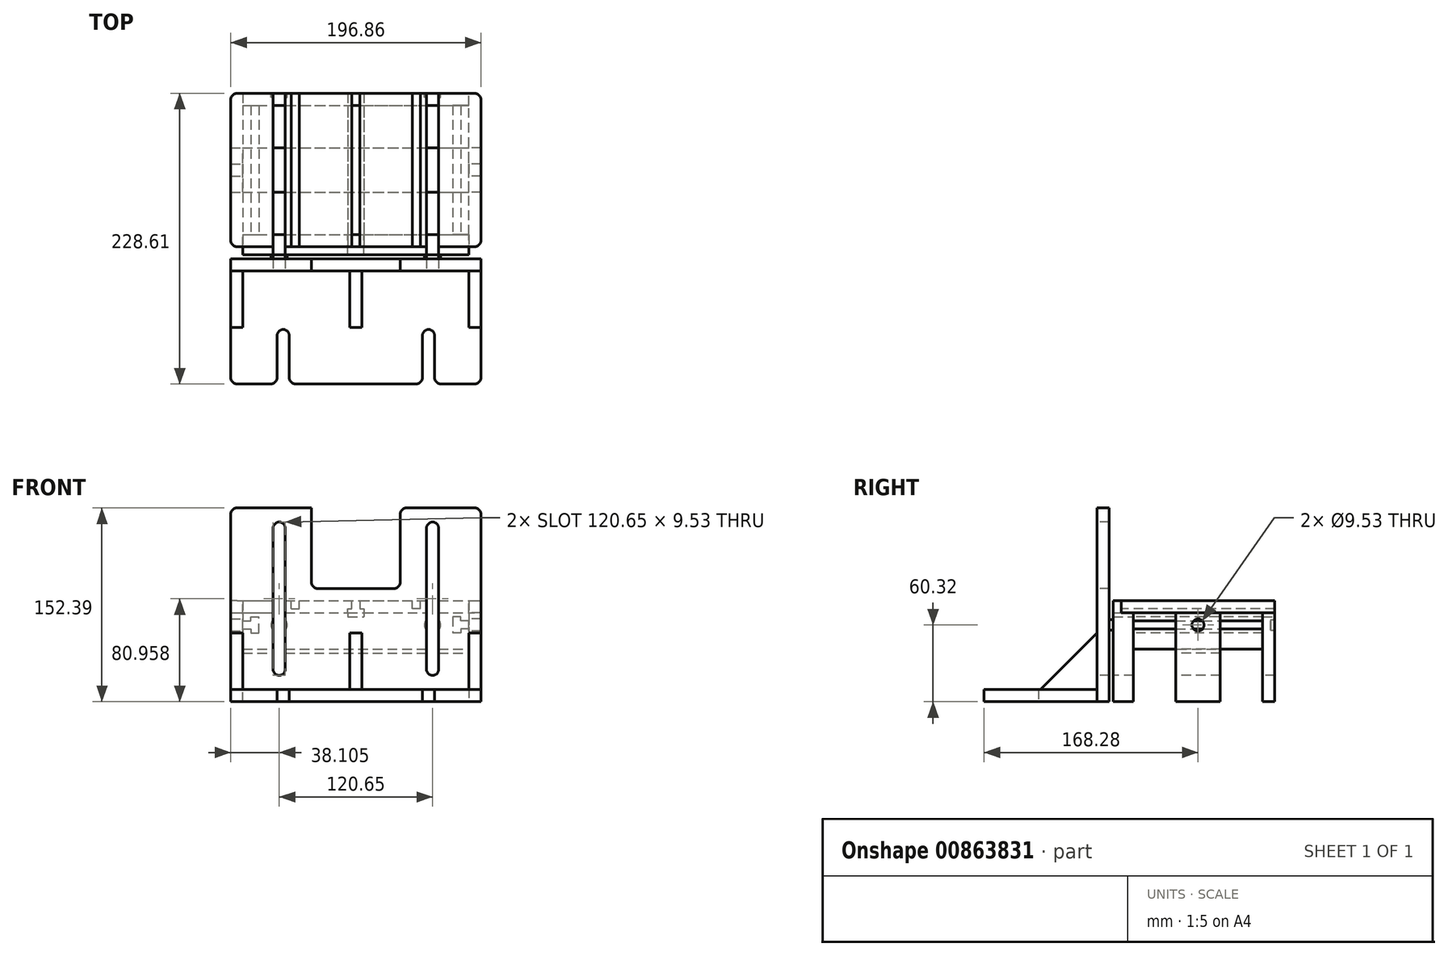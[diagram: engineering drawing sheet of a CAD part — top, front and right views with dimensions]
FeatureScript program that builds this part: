
annotation { "Feature Type Name" : "Feature", "Feature Type Description" : "" }
export const myFeature = defineFeature(function(context is Context, id is Id, definition is map)
    precondition{}
    {
        {
            var Q0;
            Q0=qCreatedBy(makeId("Top.planeOp"),FACE);
            var sketch = newSketch(context, id + "F0", { "sketchPlane" : qUnion([Q0])});
            skLineSegment(sketch, "E0.bottom", {"start": v(-98.42, 60.33) * mm, "end": v(98.43, 60.33) * mm});
            skLineSegment(sketch, "E0.top", {"start": v(-98.43, -60.33) * mm, "end": v(98.42, -60.33) * mm});
            skLineSegment(sketch, "E0.left", {"start": v(-98.42, 60.32) * mm, "end": v(-98.43, -60.33) * mm});
            skLineSegment(sketch, "E0.right", {"start": v(98.43, 60.33) * mm, "end": v(98.42, -60.33) * mm});
            skLineSegment(sketch, "E1", {"start": v(-98.43, 60.33) * mm, "end": v(98.43, -60.33) * mm, "construction": true});
            skSolve(sketch);
        }
        {
            var Q0;
            Q0=qSketchRegion(id+"F0",true);
            extrude(context, id + "F1", {"entities" : qUnion([Q0]), "depth" : 38.1 * mm});
        }
        {
            var Q0;
            Q0=makeQuery(id+"F1.opExtrude","SWEPT_FACE",FACE,{"disambiguationData":[OSD([sQuery(id+"F0.wireOp",EDGE,"E0.top")])]});
            var sketch = newSketch(context, id + "F2", { "sketchPlane" : qUnion([Q0])});
            skLineSegment(sketch, "E2", {"start": v(-98.43, 19.05) * mm, "end": v(98.43, 19.05) * mm, "construction": true});
            skLineSegment(sketch, "E3", {"start": v(0, 38.1) * mm, "end": v(0, 0) * mm, "construction": true});
            skLineSegment(sketch, "E4", {"start": v(-98.43, 19.05) * mm, "end": v(-98.43, 22.23) * mm});
            skLineSegment(sketch, "E5", {"start": v(-98.43, 22.23) * mm, "end": v(-82.55, 22.23) * mm});
            skLineSegment(sketch, "E6", {"start": v(-82.55, 22.23) * mm, "end": v(-82.55, 25.4) * mm});
            skLineSegment(sketch, "E7", {"start": v(-82.55, 25.4) * mm, "end": v(-76.2, 25.4) * mm});
            skLineSegment(sketch, "E8", {"start": v(-76.2, 25.4) * mm, "end": v(-76.2, 19.05) * mm});
            skLineSegment(sketch, "E9.MirrorCS", {"start": v(-82.55, 15.88) * mm, "end": v(-82.55, 12.7) * mm});
            skLineSegment(sketch, "E10.MirrorCS", {"start": v(-76.2, 12.7) * mm, "end": v(-76.2, 19.05) * mm});
            skLineSegment(sketch, "E11.MirrorCS", {"start": v(-82.55, 12.7) * mm, "end": v(-76.2, 12.7) * mm});
            skLineSegment(sketch, "E12.MirrorCS", {"start": v(-98.43, 15.88) * mm, "end": v(-82.55, 15.88) * mm});
            skLineSegment(sketch, "E13.MirrorCS", {"start": v(-98.43, 19.05) * mm, "end": v(-98.43, 15.88) * mm});
            skLineSegment(sketch, "E14.MirrorCS", {"start": v(82.55, 22.23) * mm, "end": v(82.55, 25.4) * mm});
            skLineSegment(sketch, "E15.MirrorCS", {"start": v(98.43, 19.05) * mm, "end": v(98.43, 15.87) * mm});
            skLineSegment(sketch, "E16.MirrorCS", {"start": v(76.2, 25.4) * mm, "end": v(76.2, 19.05) * mm});
            skLineSegment(sketch, "E17.MirrorCS", {"start": v(82.55, 25.4) * mm, "end": v(76.2, 25.4) * mm});
            skLineSegment(sketch, "E18.MirrorCS", {"start": v(98.43, 22.23) * mm, "end": v(82.55, 22.23) * mm});
            skLineSegment(sketch, "E19.MirrorCS", {"start": v(98.43, 19.05) * mm, "end": v(98.43, 22.23) * mm});
            skLineSegment(sketch, "E20.MirrorCS", {"start": v(82.55, 15.88) * mm, "end": v(82.55, 12.7) * mm});
            skLineSegment(sketch, "E21.MirrorCS", {"start": v(76.2, 12.7) * mm, "end": v(76.2, 19.05) * mm});
            skLineSegment(sketch, "E22.MirrorCS", {"start": v(98.43, 15.88) * mm, "end": v(82.55, 15.88) * mm});
            skLineSegment(sketch, "E23.MirrorCS", {"start": v(82.55, 12.7) * mm, "end": v(76.2, 12.7) * mm});
            skLineSegment(sketch, "E24", {"start": v(-3.18, 38.1) * mm, "end": v(-3.18, 31.75) * mm});
            skLineSegment(sketch, "E25", {"start": v(-3.18, 31.75) * mm, "end": v(-6.35, 31.75) * mm});
            skLineSegment(sketch, "E26", {"start": v(-6.35, 31.75) * mm, "end": v(-6.35, 25.4) * mm});
            skLineSegment(sketch, "E27", {"start": v(-6.35, 25.4) * mm, "end": v(0, 25.4) * mm});
            skLineSegment(sketch, "E28", {"start": v(0, 38.1) * mm, "end": v(-3.18, 38.1) * mm});
            skLineSegment(sketch, "E29.MirrorCS", {"start": v(3.17, 31.75) * mm, "end": v(6.35, 31.75) * mm});
            skLineSegment(sketch, "E30.MirrorCS", {"start": v(0, 38.1) * mm, "end": v(3.17, 38.1) * mm});
            skLineSegment(sketch, "E31.MirrorCS", {"start": v(6.35, 31.75) * mm, "end": v(6.35, 25.4) * mm});
            skLineSegment(sketch, "E32.MirrorCS", {"start": v(6.35, 25.4) * mm, "end": v(0, 25.4) * mm});
            skLineSegment(sketch, "E33.MirrorCS", {"start": v(3.17, 38.1) * mm, "end": v(3.17, 31.75) * mm});
            skSolve(sketch);
        }
        {
            var Q0;
            Q0=qSketchRegion(id+"F2",true);
            extrude(context, id + "F3", {"entities" : qUnion([Q0]), "operationType" : NewBodyOperationType.REMOVE, "endBound" : BoundingType.THROUGH_ALL, "oppositeDirection" : true, "depth" : 25.4 * mm});
        }
        {
            var Q0;
            Q0=makeQuery(id+"F1.opExtrude","CAP_FACE",FACE,{"disambiguationData":[OSD([sQuery(id+"F0.wireOp",EDGE,"E0.bottom"),sQuery(id+"F0.wireOp",EDGE,"E0.top"),sQuery(id+"F0.wireOp",EDGE,"E0.left"),sQuery(id+"F0.wireOp",EDGE,"E0.right")])],"isStart":true});
            var sketch = newSketch(context, id + "F4", { "sketchPlane" : qUnion([Q0])});
            skLineSegment(sketch, "E34.0", {"start": v(-88.9, 50.8) * mm, "end": v(88.9, 50.8) * mm});
            skLineSegment(sketch, "E34.1", {"start": v(-88.9, -50.8) * mm, "end": v(-88.9, 50.8) * mm});
            skLineSegment(sketch, "E34.2", {"start": v(-88.9, -50.8) * mm, "end": v(88.9, -50.8) * mm});
            skLineSegment(sketch, "E34.3", {"start": v(88.9, -50.8) * mm, "end": v(88.9, 50.8) * mm});
            skSolve(sketch);
        }
        {
            var Q0;
            Q0=makeQuery(id+"F4.imprint","IMPRINT",FACE,{"disambiguationData":[TD([[makeQuery(id+"F4.imprint","IMPRINT",EDGE,{"derivedFrom":sQuery(id+"F4.wireOp",EDGE,"E34.0")}),1.0]])]});
            var Q1;
            Q1=makeQuery(id+"F1.opExtrude","CAP_FACE",FACE,{"disambiguationData":[OSD([sQuery(id+"F0.wireOp",EDGE,"E0.bottom"),sQuery(id+"F0.wireOp",EDGE,"E0.top"),sQuery(id+"F0.wireOp",EDGE,"E0.left"),sQuery(id+"F0.wireOp",EDGE,"E0.right")])],"isStart":false});
            extrude(context, id + "F5", {"entities" : qUnion([Q0]), "operationType" : NewBodyOperationType.REMOVE, "oppositeDirection" : true, "endBoundEntityFace" : qUnion([Q1]), "depth" : 28.57 * mm});
        }
        {
            var Q0;
            {var subQ0=sQuery(id+"F0.wireOp",EDGE,"E0.bottom");var subQ1=sQuery(id+"F0.wireOp",EDGE,"E0.top");var subQ2=sQuery(id+"F0.wireOp",EDGE,"E0.left");Q0=makeQuery(id+"F3.boolean.opBoolean","SPLIT",FACE,{"disambiguationData":[TD([makeQuery(id+"F1.opExtrude","SWEPT_FACE",FACE,{"disambiguationData":[OSD([subQ2])]})])],"derivedFrom":makeQuery(id+"F1.opExtrude","CAP_FACE",FACE,{"disambiguationData":[OSD([subQ0,subQ1,subQ2,sQuery(id+"F0.wireOp",EDGE,"E0.right")])],"isStart":false})});}
            var sketch = newSketch(context, id + "F6", { "sketchPlane" : qUnion([Q0])});
            skLineSegment(sketch, "E35.bottom", {"start": v(-50.8, 60.33) * mm, "end": v(-44.45, 60.33) * mm});
            skLineSegment(sketch, "E35.top", {"start": v(-50.8, -60.33) * mm, "end": v(-44.45, -60.33) * mm});
            skLineSegment(sketch, "E35.left", {"start": v(-50.8, 60.33) * mm, "end": v(-50.8, -60.33) * mm});
            skLineSegment(sketch, "E35.right", {"start": v(-44.45, 60.33) * mm, "end": v(-44.45, -60.33) * mm});
            skLineSegment(sketch, "E36", {"start": v(-47.63, 60.33) * mm, "end": v(-47.62, -60.33) * mm, "construction": true});
            skLineSegment(sketch, "E37", {"start": v(-98.43, 60.33) * mm, "end": v(98.43, -60.33) * mm, "construction": true});
            skLineSegment(sketch, "E38", {"start": v(0, 0) * mm, "end": v(0, 29.12) * mm, "construction": true});
            skLineSegment(sketch, "E39.MirrorCS", {"start": v(50.8, -60.33) * mm, "end": v(44.45, -60.33) * mm});
            skLineSegment(sketch, "E40.MirrorCS", {"start": v(50.8, 60.33) * mm, "end": v(44.45, 60.33) * mm});
            skLineSegment(sketch, "E41.MirrorCS", {"start": v(44.45, 60.33) * mm, "end": v(44.45, -60.33) * mm});
            skLineSegment(sketch, "E42.MirrorCS", {"start": v(50.8, 60.33) * mm, "end": v(50.8, -60.33) * mm});
            skSolve(sketch);
        }
        {
            var Q0;
            Q0=qSketchRegion(id+"F6",true);
            extrude(context, id + "F7", {"entities" : qUnion([Q0]), "operationType" : NewBodyOperationType.REMOVE, "oppositeDirection" : true, "depth" : 6.35 * mm});
        }
        {
            var Q0;
            {var subQ0=sQuery(id+"F0.wireOp",EDGE,"E0.bottom");var subQ2=sQuery(id+"F0.wireOp",EDGE,"E0.top");var subQ4=sQuery(id+"F0.wireOp",EDGE,"E0.left");var subQ5=makeQuery(id+"F1.opExtrude","SWEPT_FACE",FACE,{"disambiguationData":[OSD([subQ4])]});Q0=makeQuery(id+"F7.boolean.opBoolean","SPLIT",FACE,{"disambiguationData":[TD([subQ5])],"derivedFrom":makeQuery(id+"F3.boolean.opBoolean","SPLIT",FACE,{"disambiguationData":[TD([subQ5])],"derivedFrom":makeQuery(id+"F1.opExtrude","CAP_FACE",FACE,{"disambiguationData":[OSD([subQ0,subQ2,subQ4,sQuery(id+"F0.wireOp",EDGE,"E0.right")])],"isStart":false})})});}
            var sketch = newSketch(context, id + "F8", { "sketchPlane" : qUnion([Q0])});
            skCircle(sketch, "E43", {"center": v(-60.33, 22.23) * mm, "radius": 4.76 * mm});
            skLineSegment(sketch, "E44", {"start": v(-98.43, 0) * mm, "end": v(98.43, 0) * mm, "construction": true});
            skLineSegment(sketch, "E45", {"start": v(0, 0) * mm, "end": v(0, 12.86) * mm, "construction": true});
            skCircle(sketch, "E46.MirrorC", {"center": v(-60.33, -22.23) * mm, "radius": 4.76 * mm});
            skCircle(sketch, "E47.MirrorC", {"center": v(60.33, -22.22) * mm, "radius": 4.76 * mm});
            skCircle(sketch, "E48.MirrorC", {"center": v(60.33, 22.22) * mm, "radius": 4.76 * mm});
            skSolve(sketch);
        }
        {
            var Q0;
            Q0=qSketchRegion(id+"F8",true);
            extrude(context, id + "F9", {"entities" : qUnion([Q0]), "operationType" : NewBodyOperationType.REMOVE, "oppositeDirection" : true, "depth" : 19.05 * mm});
        }
        {
            var Q0;
            Q0=makeQuery(id+"F5.boolean.opBoolean","COPY",FACE,{"disambiguationData":[TD([makeQuery(id+"F3.boolean.opBoolean","COPY",FACE,{"derivedFrom":makeQuery(id+"F3.opExtrude","SWEPT_FACE",FACE,{"disambiguationData":[OSD([sQuery(id+"F2.wireOp",EDGE,"E22.MirrorCS")])]})})])],"derivedFrom":makeQuery(id+"F5.opExtrude","SWEPT_FACE",FACE,{"disambiguationData":[OSD([sQuery(id+"F4.wireOp",EDGE,"E34.3")])]})});
            var sketch = newSketch(context, id + "F10", { "sketchPlane" : qUnion([Q0])});
            skLineSegment(sketch, "E49", {"start": v(-50.8, 28.58) * mm, "end": v(-60.33, 28.58) * mm});
            skLineSegment(sketch, "E50", {"start": v(-60.33, 28.58) * mm, "end": v(-60.33, 38.1) * mm});
            skLineSegment(sketch, "E51", {"start": v(-60.33, 38.1) * mm, "end": v(-69.85, 38.1) * mm});
            skLineSegment(sketch, "E52", {"start": v(-69.85, 38.1) * mm, "end": v(-69.85, -41.28) * mm});
            skLineSegment(sketch, "E53", {"start": v(-69.85, -41.28) * mm, "end": v(-50.8, -41.28) * mm});
            skLineSegment(sketch, "E54", {"start": v(-50.8, -41.28) * mm, "end": v(-50.8, 28.58) * mm});
            skLineSegment(sketch, "E55.bottom", {"start": v(50.8, 28.58) * mm, "end": v(60.33, 28.58) * mm});
            skLineSegment(sketch, "E55.top", {"start": v(50.8, -41.28) * mm, "end": v(60.33, -41.28) * mm});
            skLineSegment(sketch, "E55.left", {"start": v(50.8, 28.58) * mm, "end": v(50.8, -41.28) * mm});
            skLineSegment(sketch, "E55.right", {"start": v(60.33, 28.58) * mm, "end": v(60.33, -41.28) * mm});
            skSolve(sketch);
        }
        {
            var Q0;
            Q0=qSketchRegion(id+"F10",true);
            var Q1;
            Q1=makeQuery(id+"F5.boolean.opBoolean","COPY",FACE,{"disambiguationData":[TD([makeQuery(id+"F3.boolean.opBoolean","COPY",FACE,{"derivedFrom":makeQuery(id+"F3.opExtrude","SWEPT_FACE",FACE,{"disambiguationData":[OSD([sQuery(id+"F2.wireOp",EDGE,"E12.MirrorCS")])]})})])],"derivedFrom":makeQuery(id+"F5.opExtrude","SWEPT_FACE",FACE,{"disambiguationData":[OSD([sQuery(id+"F4.wireOp",EDGE,"E34.1")])]})});
            extrude(context, id + "F11", {"entities" : qUnion([Q0]), "endBound" : BoundingType.UP_TO_SURFACE, "oppositeDirection" : true, "endBoundEntityFace" : qUnion([Q1]), "depth" : 25.4 * mm});
        }
        {
            var Q0;
            Q0=makeQuery(id+"F11.opExtrude","SWEPT_FACE",FACE,{"disambiguationData":[OSD([sQuery(id+"F10.wireOp",EDGE,"E55.right")])]});
            var sketch = newSketch(context, id + "F12", { "sketchPlane" : qUnion([Q0])});
            skCircle(sketch, "E56", {"center": v(-60.33, 19.05) * mm, "radius": 4.76 * mm});
            skCircle(sketch, "E57", {"center": v(60.33, 19.05) * mm, "radius": 4.76 * mm});
            skLineSegment(sketch, "E58", {"start": v(-60.33, 19.05) * mm, "end": v(60.33, 19.05) * mm, "construction": true});
            skLineSegment(sketch, "E59", {"start": v(0, 28.58) * mm, "end": v(0, 3.82) * mm, "construction": true});
            skCircle(sketch, "E60", {"center": v(-60.33, 19.05) * mm, "radius": 6.35 * mm});
            skCircle(sketch, "E61", {"center": v(60.33, 19.05) * mm, "radius": 6.35 * mm});
            skLineSegment(sketch, "E62.0", {"start": v(-6.35, 28.57) * mm, "end": v(-6.35, 25.4) * mm});
            skLineSegment(sketch, "E62.1", {"start": v(6.35, 25.4) * mm, "end": v(-6.35, 25.4) * mm});
            skLineSegment(sketch, "E62.2", {"start": v(6.35, 28.57) * mm, "end": v(6.35, 25.4) * mm});
            skLineSegment(sketch, "E63", {"start": v(-6.35, 28.57) * mm, "end": v(6.35, 28.57) * mm});
            skSolve(sketch);
        }
        {
            var Q0;
            Q0=makeQuery(id+"F12.imprint","IMPRINT",FACE,{"disambiguationData":[TD([[makeQuery(id+"F12.imprint","IMPRINT",EDGE,{"derivedFrom":sQuery(id+"F12.wireOp",EDGE,"E56")}),-1.0]])]});
            var Q1;
            Q1=makeQuery(id+"F12.imprint","IMPRINT",FACE,{"disambiguationData":[TD([[makeQuery(id+"F12.imprint","IMPRINT",EDGE,{"derivedFrom":sQuery(id+"F12.wireOp",EDGE,"E56")}),1.0]])]});
            var Q2;
            Q2=makeQuery(id+"F12.imprint","IMPRINT",FACE,{"disambiguationData":[TD([[makeQuery(id+"F12.imprint","IMPRINT",EDGE,{"derivedFrom":sQuery(id+"F12.wireOp",EDGE,"E57")}),-1.0]])]});
            var Q3;
            Q3=makeQuery(id+"F12.imprint","IMPRINT",FACE,{"disambiguationData":[TD([[makeQuery(id+"F12.imprint","IMPRINT",EDGE,{"derivedFrom":sQuery(id+"F12.wireOp",EDGE,"E57")}),1.0]])]});
            var Q4;
            Q4=sQuery(id+"F12.wireOp",EDGE,"E60");
            var Q5;
            Q5=sQuery(id+"F12.wireOp",EDGE,"E61");
            extrude(context, id + "F13", {"entities" : qUnion([Q0, Q1, Q2, Q3]), "operationType" : NewBodyOperationType.REMOVE, "surfaceEntities" : qUnion([Q4, Q5]), "oppositeDirection" : true, "depth" : 3.17 * mm});
        }
        {
            var Q0;
            Q0=makeQuery(id+"F12.imprint","IMPRINT",FACE,{"disambiguationData":[TD([[makeQuery(id+"F12.imprint","IMPRINT",EDGE,{"derivedFrom":sQuery(id+"F12.wireOp",EDGE,"E56")}),1.0]])]});
            var Q1;
            Q1=makeQuery(id+"F12.imprint","IMPRINT",FACE,{"disambiguationData":[TD([[makeQuery(id+"F12.imprint","IMPRINT",EDGE,{"derivedFrom":sQuery(id+"F12.wireOp",EDGE,"E57")}),1.0]])]});
            var Q2;
            Q2=sQuery(id+"F12.wireOp",EDGE,"E56");
            var Q3;
            Q3=sQuery(id+"F12.wireOp",EDGE,"E57");
            extrude(context, id + "F14", {"entities" : qUnion([Q0, Q1]), "operationType" : NewBodyOperationType.REMOVE, "surfaceEntities" : qUnion([Q2, Q3]), "endBound" : BoundingType.THROUGH_ALL, "oppositeDirection" : true, "depth" : 25.4 * mm});
        }
        {
            var Q0;
            Q0=makeQuery(id+"F11.opExtrude","SWEPT_FACE",FACE,{"disambiguationData":[OSD([sQuery(id+"F10.wireOp",EDGE,"E52")])]});
            var sketch = newSketch(context, id + "F15", { "sketchPlane" : qUnion([Q0])});
            skCircle(sketch, "E64.0", {"center": v(-60.33, 19.05) * mm, "radius": 6.35 * mm});
            skCircle(sketch, "E64.1", {"center": v(60.33, 19.05) * mm, "radius": 6.35 * mm});
            skCircle(sketch, "E65", {"center": v(-60.32, -12.7) * mm, "radius": 4.76 * mm});
            skCircle(sketch, "E66", {"center": v(60.33, -12.7) * mm, "radius": 4.76 * mm});
            skSolve(sketch);
        }
        {
            var Q0;
            Q0=makeQuery(id+"F15.imprint","IMPRINT",FACE,{"disambiguationData":[TD([[makeQuery(id+"F15.imprint","IMPRINT",EDGE,{"derivedFrom":makeQuery(id+"F14.boolean.opBoolean","INTERSECT",EDGE,{"derivedFrom":[makeQuery(id+"F11.opExtrude","SWEPT_FACE",FACE,{"disambiguationData":[OSD([sQuery(id+"F10.wireOp",EDGE,"E52")])]}),makeQuery(id+"F14.opExtrude","SWEPT_FACE",FACE,{"disambiguationData":[OSD([sQuery(id+"F12.wireOp",EDGE,"E56")])]})]})}),1.0]])]});
            var Q1;
            Q1=makeQuery(id+"F15.imprint","IMPRINT",FACE,{"disambiguationData":[TD([[makeQuery(id+"F15.imprint","IMPRINT",EDGE,{"derivedFrom":makeQuery(id+"F14.boolean.opBoolean","INTERSECT",EDGE,{"derivedFrom":[makeQuery(id+"F11.opExtrude","SWEPT_FACE",FACE,{"disambiguationData":[OSD([sQuery(id+"F10.wireOp",EDGE,"E52")])]}),makeQuery(id+"F14.opExtrude","SWEPT_FACE",FACE,{"disambiguationData":[OSD([sQuery(id+"F12.wireOp",EDGE,"E57")])]})]})}),1.0]])]});
            var Q2;
            Q2=makeQuery(id+"F15.imprint","IMPRINT",FACE,{"disambiguationData":[TD([[makeQuery(id+"F15.imprint","IMPRINT",EDGE,{"derivedFrom":sQuery(id+"F15.wireOp",EDGE,"E64.0")}),-1.0]])]});
            var Q3;
            Q3=makeQuery(id+"F15.imprint","IMPRINT",FACE,{"disambiguationData":[TD([[makeQuery(id+"F15.imprint","IMPRINT",EDGE,{"derivedFrom":sQuery(id+"F15.wireOp",EDGE,"E64.1")}),-1.0]])]});
            extrude(context, id + "F16", {"entities" : qUnion([Q0, Q1, Q2, Q3]), "operationType" : NewBodyOperationType.REMOVE, "oppositeDirection" : true, "depth" : 3.17 * mm});
        }
        {
            var Q0;
            Q0=makeQuery(id+"F15.imprint","IMPRINT",FACE,{"disambiguationData":[TD([[makeQuery(id+"F15.imprint","IMPRINT",EDGE,{"derivedFrom":sQuery(id+"F15.wireOp",EDGE,"E65")}),1.0]])]});
            var Q1;
            Q1=makeQuery(id+"F15.imprint","IMPRINT",FACE,{"disambiguationData":[TD([[makeQuery(id+"F15.imprint","IMPRINT",EDGE,{"derivedFrom":sQuery(id+"F15.wireOp",EDGE,"E66")}),1.0]])]});
            var Q2;
            Q2=makeQuery(id+"F11.opExtrude","SWEPT_FACE",FACE,{"disambiguationData":[OSD([sQuery(id+"F10.wireOp",EDGE,"E54")])]});
            extrude(context, id + "F17", {"entities" : qUnion([Q0, Q1]), "operationType" : NewBodyOperationType.REMOVE, "endBound" : BoundingType.UP_TO_SURFACE, "oppositeDirection" : true, "endBoundEntityFace" : qUnion([Q2]), "depth" : 25.4 * mm});
        }
        {
            var Q0;
            Q0=makeQuery(id+"F12.imprint","IMPRINT",FACE,{"disambiguationData":[TD([[makeQuery(id+"F12.imprint","IMPRINT",EDGE,{"derivedFrom":sQuery(id+"F12.wireOp",EDGE,"E62.0")}),1.0]])]});
            extrude(context, id + "F18", {"entities" : qUnion([Q0]), "operationType" : NewBodyOperationType.REMOVE, "endBound" : BoundingType.THROUGH_ALL, "oppositeDirection" : true, "depth" : 25.4 * mm});
        }
        {
            var Q0;
            Q0=makeQuery(id+"F5.boolean.opBoolean","COPY",FACE,{"disambiguationData":[TD([makeQuery(id+"F3.boolean.opBoolean","COPY",FACE,{"derivedFrom":makeQuery(id+"F3.opExtrude","SWEPT_FACE",FACE,{"disambiguationData":[OSD([sQuery(id+"F2.wireOp",EDGE,"E22.MirrorCS")])]})})])],"derivedFrom":makeQuery(id+"F5.opExtrude","SWEPT_FACE",FACE,{"disambiguationData":[OSD([sQuery(id+"F4.wireOp",EDGE,"E34.3")])]})});
            var sketch = newSketch(context, id + "F19", { "sketchPlane" : qUnion([Q0])});
            skLineSegment(sketch, "E67.top", {"start": v(-17.46, -41.28) * mm, "end": v(17.46, -41.28) * mm});
            skLineSegment(sketch, "E67.left", {"start": v(-17.46, -3.18) * mm, "end": v(-17.46, -41.28) * mm});
            skLineSegment(sketch, "E67.right", {"start": v(17.46, -3.17) * mm, "end": v(17.46, -41.27) * mm});
            skLineSegment(sketch, "E68", {"start": v(0, 15.88) * mm, "end": v(0, -3.18) * mm, "construction": true});
            skLineSegment(sketch, "E69", {"start": v(-17.46, -3.18) * mm, "end": v(17.46, -3.18) * mm});
            skSolve(sketch);
        }
        {
            var Q0;
            Q0=qSketchRegion(id+"F19",true);
            var Q1;
            Q1=makeQuery(id+"F5.boolean.opBoolean","COPY",FACE,{"disambiguationData":[TD([makeQuery(id+"F3.boolean.opBoolean","COPY",FACE,{"derivedFrom":makeQuery(id+"F3.opExtrude","SWEPT_FACE",FACE,{"disambiguationData":[OSD([sQuery(id+"F2.wireOp",EDGE,"E12.MirrorCS")])]})})])],"derivedFrom":makeQuery(id+"F5.opExtrude","SWEPT_FACE",FACE,{"disambiguationData":[OSD([sQuery(id+"F4.wireOp",EDGE,"E34.1")])]})});
            extrude(context, id + "F20", {"entities" : qUnion([Q0]), "endBound" : BoundingType.UP_TO_SURFACE, "oppositeDirection" : true, "endBoundEntityFace" : qUnion([Q1]), "depth" : 25.4 * mm});
        }
        {
            var Q0;
            Q0=makeQuery(id+"F20.opExtrude","CAP_FACE",FACE,{"disambiguationData":[OSD([sQuery(id+"F19.wireOp",EDGE,"E67.bottom"),sQuery(id+"F19.wireOp",EDGE,"E67.top"),sQuery(id+"F19.wireOp",EDGE,"E67.left"),sQuery(id+"F19.wireOp",EDGE,"E67.right")])],"isStart":true});
            var sketch = newSketch(context, id + "F21", { "sketchPlane" : qUnion([Q0])});
            skLineSegment(sketch, "E70.bottom", {"start": v(-17.46, -41.28) * mm, "end": v(17.46, -41.28) * mm});
            skLineSegment(sketch, "E70.top", {"start": v(-17.46, 28.58) * mm, "end": v(17.46, 28.58) * mm});
            skLineSegment(sketch, "E70.left", {"start": v(-17.46, -41.28) * mm, "end": v(-17.46, 28.58) * mm});
            skLineSegment(sketch, "E70.right", {"start": v(17.46, -41.28) * mm, "end": v(17.46, 28.58) * mm});
            skLineSegment(sketch, "E71", {"start": v(-17.46, 15.88) * mm, "end": v(17.46, 22.23) * mm, "construction": true});
            skCircle(sketch, "E72", {"center": v(0, 19.05) * mm, "radius": 4.76 * mm});
            skSolve(sketch);
        }
        {
            var Q0;
            Q0=qSketchRegion(id+"F21",true);
            extrude(context, id + "F22", {"entities" : qUnion([Q0]), "depth" : 9.52 * mm});
        }
        {
            var Q0;
            Q0=makeQuery(id+"F22.opExtrude","SWEPT_BODY",BODY,{"disambiguationData":[OSD([sQuery(id+"F21.wireOp",EDGE,"E70.bottom"),sQuery(id+"F21.wireOp",EDGE,"E70.top"),sQuery(id+"F21.wireOp",EDGE,"E70.left"),sQuery(id+"F21.wireOp",EDGE,"E70.right"),sQuery(id+"F21.wireOp",EDGE,"E72")])]});
            var Q1;
            Q1=qCreatedBy(makeId("Right.planeOp"),FACE);
            mirror(context, id + "F23", {"entities" : qUnion([Q0]), "mirrorPlane" : qUnion([Q1])});
        }
        {
            var Q0;
            Q0=makeQuery(id+"F11.opExtrude","SWEPT_FACE",FACE,{"disambiguationData":[OSD([sQuery(id+"F10.wireOp",EDGE,"E52")])]});
            var sketch = newSketch(context, id + "F24", { "sketchPlane" : qUnion([Q0])});
            skLineSegment(sketch, "E73.bottom", {"start": v(-98.43, 111.13) * mm, "end": v(98.43, 111.13) * mm});
            skLineSegment(sketch, "E73.top", {"start": v(-98.43, -41.27) * mm, "end": v(98.43, -41.27) * mm});
            skLineSegment(sketch, "E73.left", {"start": v(-98.43, 111.13) * mm, "end": v(-98.43, -41.27) * mm});
            skLineSegment(sketch, "E73.right", {"start": v(98.43, 111.13) * mm, "end": v(98.43, -41.27) * mm});
            skSolve(sketch);
        }
        {
            var Q0;
            Q0=qSketchRegion(id+"F24",true);
            extrude(context, id + "F25", {"entities" : qUnion([Q0]), "depth" : 9.52 * mm});
        }
        {
            var Q0;
            Q0=makeQuery(id+"F25.opExtrude","CAP_FACE",FACE,{"disambiguationData":[OSD([sQuery(id+"F24.wireOp",EDGE,"E73.bottom"),sQuery(id+"F24.wireOp",EDGE,"E73.top"),sQuery(id+"F24.wireOp",EDGE,"E73.left"),sQuery(id+"F24.wireOp",EDGE,"E73.right")])],"isStart":false});
            var sketch = newSketch(context, id + "F26", { "sketchPlane" : qUnion([Q0])});
            skLineSegment(sketch, "E74.left", {"start": v(-55.56, -15.88) * mm, "end": v(-55.56, 95.25) * mm});
            skLineSegment(sketch, "E74.right", {"start": v(-65.09, -15.88) * mm, "end": v(-65.09, 95.25) * mm});
            skPoint(sketch, "E74.middle", {"position": v(-60.33, 39.69) * mm});
            skArc(sketch, "E75", {"start": v(-55.56, 95.25) * mm, "mid": v(-60.33, 100.01) * mm, "end": v(-65.09, 95.25) * mm});
            skArc(sketch, "E76", {"start": v(-65.09, -15.87) * mm, "mid": v(-60.33, -20.64) * mm, "end": v(-55.56, -15.87) * mm});
            skLineSegment(sketch, "E77", {"start": v(0, 111.13) * mm, "end": v(0, -41.28) * mm, "construction": true});
            skLineSegment(sketch, "E78.MirrorCS", {"start": v(55.56, -15.87) * mm, "end": v(55.56, 95.25) * mm});
            skLineSegment(sketch, "E79.MirrorCS", {"start": v(65.09, -15.87) * mm, "end": v(65.09, 95.25) * mm});
            skArc(sketch, "E80.MirrorCS", {"start": v(55.56, 95.25) * mm, "mid": v(60.33, 100.01) * mm, "end": v(65.09, 95.25) * mm});
            skPoint(sketch, "E81.MirrorP", {"position": v(60.33, 39.69) * mm});
            skArc(sketch, "E82.MirrorCS", {"start": v(65.09, -15.87) * mm, "mid": v(60.33, -20.64) * mm, "end": v(55.56, -15.87) * mm});
            skLineSegment(sketch, "E83.bottom", {"start": v(-34.93, 111.13) * mm, "end": v(34.93, 111.13) * mm});
            skLineSegment(sketch, "E83.top", {"start": v(-34.93, 47.63) * mm, "end": v(34.93, 47.63) * mm});
            skLineSegment(sketch, "E83.left", {"start": v(-34.93, 111.13) * mm, "end": v(-34.93, 47.63) * mm});
            skLineSegment(sketch, "E83.right", {"start": v(34.93, 111.13) * mm, "end": v(34.93, 47.63) * mm});
            skSolve(sketch);
        }
        {
            var Q0;
            Q0=qSketchRegion(id+"F26",true);
            extrude(context, id + "F27", {"entities" : qUnion([Q0]), "operationType" : NewBodyOperationType.REMOVE, "endBound" : BoundingType.THROUGH_ALL, "oppositeDirection" : true, "depth" : 25.4 * mm});
        }
        {
            var Q0;
            Q0=makeQuery(id+"F25.opExtrude","CAP_FACE",FACE,{"disambiguationData":[OSD([sQuery(id+"F24.wireOp",EDGE,"E73.bottom"),sQuery(id+"F24.wireOp",EDGE,"E73.top"),sQuery(id+"F24.wireOp",EDGE,"E73.left"),sQuery(id+"F24.wireOp",EDGE,"E73.right")])],"isStart":false});
            var sketch = newSketch(context, id + "F28", { "sketchPlane" : qUnion([Q0])});
            skLineSegment(sketch, "E84.bottom", {"start": v(-98.43, -31.75) * mm, "end": v(-88.9, -31.75) * mm});
            skLineSegment(sketch, "E84.top", {"start": v(-98.43, 12.7) * mm, "end": v(-88.9, 12.7) * mm});
            skLineSegment(sketch, "E84.left", {"start": v(-98.43, -31.75) * mm, "end": v(-98.43, 12.7) * mm});
            skLineSegment(sketch, "E84.right", {"start": v(-88.9, -31.75) * mm, "end": v(-88.9, 12.7) * mm});
            skLineSegment(sketch, "E85.bottom", {"start": v(98.43, -31.75) * mm, "end": v(88.9, -31.75) * mm});
            skLineSegment(sketch, "E85.top", {"start": v(98.43, 12.7) * mm, "end": v(88.9, 12.7) * mm});
            skLineSegment(sketch, "E85.left", {"start": v(98.43, -31.75) * mm, "end": v(98.43, 12.7) * mm});
            skLineSegment(sketch, "E85.right", {"start": v(88.9, -31.75) * mm, "end": v(88.9, 12.7) * mm});
            skLineSegment(sketch, "E86.top", {"start": v(-4.76, 12.7) * mm, "end": v(4.76, 12.7) * mm});
            skLineSegment(sketch, "E86.left", {"start": v(4.76, -31.75) * mm, "end": v(4.76, 12.7) * mm});
            skLineSegment(sketch, "E86.right", {"start": v(-4.76, -31.75) * mm, "end": v(-4.76, 12.7) * mm});
            skLineSegment(sketch, "E87", {"start": v(0, -41.27) * mm, "end": v(0, 12.7) * mm, "construction": true});
            skLineSegment(sketch, "E88", {"start": v(-4.76, -31.75) * mm, "end": v(4.76, -31.75) * mm});
            skSolve(sketch);
        }
        {
            var Q0;
            Q0=qSketchRegion(id+"F28",true);
            extrude(context, id + "F29", {"entities" : qUnion([Q0]), "depth" : 44.45 * mm});
        }
        {
            var Q0;
            Q0=makeQuery(id+"F29.opExtrude","SWEPT_FACE",FACE,{"disambiguationData":[OSD([sQuery(id+"F28.wireOp",EDGE,"E84.left")])]});
            var sketch = newSketch(context, id + "F30", { "sketchPlane" : qUnion([Q0])});
            skLineSegment(sketch, "E89", {"start": v(79.38, 12.7) * mm, "end": v(123.83, -31.75) * mm});
            skLineSegment(sketch, "E90", {"start": v(123.83, -31.75) * mm, "end": v(123.83, 12.7) * mm});
            skLineSegment(sketch, "E91", {"start": v(123.83, 12.7) * mm, "end": v(79.38, 12.7) * mm});
            skSolve(sketch);
        }
        {
            var Q0;
            Q0=qSketchRegion(id+"F30",true);
            extrude(context, id + "F31", {"entities" : qUnion([Q0]), "operationType" : NewBodyOperationType.REMOVE, "endBound" : BoundingType.THROUGH_ALL, "oppositeDirection" : true, "depth" : 25.4 * mm});
        }
        {
            var Q0;
            Q0=makeQuery(id+"F25.opExtrude","SWEPT_FACE",FACE,{"disambiguationData":[OSD([sQuery(id+"F24.wireOp",EDGE,"E73.top")])]});
            var sketch = newSketch(context, id + "F32", { "sketchPlane" : qUnion([Q0])});
            skLineSegment(sketch, "E92.bottom", {"start": v(-98.43, 79.38) * mm, "end": v(98.42, 79.38) * mm});
            skLineSegment(sketch, "E92.top", {"start": v(-98.43, 168.28) * mm, "end": v(-61.91, 168.28) * mm});
            skLineSegment(sketch, "E92.left", {"start": v(-98.43, 79.38) * mm, "end": v(-98.43, 168.28) * mm});
            skLineSegment(sketch, "E92.right", {"start": v(98.42, 79.38) * mm, "end": v(98.42, 168.28) * mm});
            skLineSegment(sketch, "E93", {"start": v(0, 168.28) * mm, "end": v(0, 131.76) * mm, "construction": true});
            skLineSegment(sketch, "E94.left", {"start": v(-52.39, 130.18) * mm, "end": v(-52.39, 168.28) * mm});
            skLineSegment(sketch, "E94.right", {"start": v(-61.91, 130.18) * mm, "end": v(-61.91, 168.28) * mm});
            skPoint(sketch, "E94.middle", {"position": v(-57.15, 149.23) * mm});
            skArc(sketch, "E95", {"start": v(-61.91, 130.18) * mm, "mid": v(-57.15, 125.41) * mm, "end": v(-52.39, 130.18) * mm});
            skLineSegment(sketch, "E96.trimOffspring", {"start": v(-52.39, 168.28) * mm, "end": v(52.39, 168.28) * mm});
            skArc(sketch, "E97.MirrorCS", {"start": v(61.91, 130.18) * mm, "mid": v(57.15, 125.41) * mm, "end": v(52.39, 130.18) * mm});
            skPoint(sketch, "E98.MirrorP", {"position": v(57.15, 149.23) * mm});
            skLineSegment(sketch, "E99.MirrorCS", {"start": v(52.39, 130.18) * mm, "end": v(52.39, 168.28) * mm});
            skLineSegment(sketch, "E100.MirrorCS", {"start": v(61.91, 130.18) * mm, "end": v(61.91, 168.28) * mm});
            skLineSegment(sketch, "E101.trimOffspring", {"start": v(61.91, 168.28) * mm, "end": v(98.42, 168.28) * mm});
            skSolve(sketch);
        }
        {
            var Q0;
            Q0=qSketchRegion(id+"F32",true);
            extrude(context, id + "F33", {"entities" : qUnion([Q0]), "oppositeDirection" : true, "depth" : 9.52 * mm});
        }
        {
            var Q0;
            Q0=makeQuery(id+"F25.opExtrude","SWEPT_EDGE",EDGE,{"disambiguationData":[OSD([sQuery(id+"F24.wireOp",EDGE,"E73.bottom"),sQuery(id+"F24.wireOp",EDGE,"E73.left")])]});
            var Q1;
            Q1=makeQuery(id+"F27.boolean.opBoolean","COPY",EDGE,{"derivedFrom":makeQuery(id+"F27.opExtrude","SWEPT_EDGE",EDGE,{"disambiguationData":[OSD([sQuery(id+"F24.wireOp",EDGE,"E73.bottom"),sQuery(id+"F26.wireOp",EDGE,"E83.bottom"),sQuery(id+"F26.wireOp",EDGE,"E83.left")])]})});
            var Q2;
            Q2=makeQuery(id+"F27.boolean.opBoolean","COPY",EDGE,{"derivedFrom":makeQuery(id+"F27.opExtrude","SWEPT_EDGE",EDGE,{"disambiguationData":[OSD([sQuery(id+"F24.wireOp",EDGE,"E73.bottom"),sQuery(id+"F26.wireOp",EDGE,"E83.bottom"),sQuery(id+"F26.wireOp",EDGE,"E83.right")])]})});
            var Q3;
            Q3=makeQuery(id+"F25.opExtrude","SWEPT_EDGE",EDGE,{"disambiguationData":[OSD([sQuery(id+"F24.wireOp",EDGE,"E73.bottom"),sQuery(id+"F24.wireOp",EDGE,"E73.right")])]});
            var Q4;
            Q4=makeQuery(id+"F27.boolean.opBoolean","COPY",EDGE,{"derivedFrom":makeQuery(id+"F27.opExtrude","SWEPT_EDGE",EDGE,{"disambiguationData":[OSD([sQuery(id+"F26.wireOp",EDGE,"E83.top"),sQuery(id+"F26.wireOp",EDGE,"E83.left")])]})});
            var Q5;
            Q5=makeQuery(id+"F27.boolean.opBoolean","COPY",EDGE,{"derivedFrom":makeQuery(id+"F27.opExtrude","SWEPT_EDGE",EDGE,{"disambiguationData":[OSD([sQuery(id+"F26.wireOp",EDGE,"E83.top"),sQuery(id+"F26.wireOp",EDGE,"E83.right")])]})});
            var Q6;
            Q6=makeQuery(id+"F33.opExtrude","SWEPT_EDGE",EDGE,{"disambiguationData":[OSD([sQuery(id+"F32.wireOp",EDGE,"E92.top"),sQuery(id+"F32.wireOp",EDGE,"E94.right")])]});
            var Q7;
            Q7=makeQuery(id+"F33.opExtrude","SWEPT_EDGE",EDGE,{"disambiguationData":[OSD([sQuery(id+"F32.wireOp",EDGE,"E94.left"),sQuery(id+"F32.wireOp",EDGE,"E96.trimOffspring")])]});
            var Q8;
            Q8=makeQuery(id+"F33.opExtrude","SWEPT_EDGE",EDGE,{"disambiguationData":[OSD([sQuery(id+"F32.wireOp",EDGE,"E96.trimOffspring"),sQuery(id+"F32.wireOp",EDGE,"E99.MirrorCS")])]});
            var Q9;
            Q9=makeQuery(id+"F33.opExtrude","SWEPT_EDGE",EDGE,{"disambiguationData":[OSD([sQuery(id+"F32.wireOp",EDGE,"E100.MirrorCS"),sQuery(id+"F32.wireOp",EDGE,"E101.trimOffspring")])]});
            var Q10;
            Q10=makeQuery(id+"F33.opExtrude","SWEPT_EDGE",EDGE,{"disambiguationData":[OSD([sQuery(id+"F32.wireOp",EDGE,"E92.top"),sQuery(id+"F32.wireOp",EDGE,"E92.left")])]});
            var Q11;
            Q11=makeQuery(id+"F33.opExtrude","SWEPT_EDGE",EDGE,{"disambiguationData":[OSD([sQuery(id+"F32.wireOp",EDGE,"E92.right"),sQuery(id+"F32.wireOp",EDGE,"E101.trimOffspring")])]});
            var Q12;
            {var subQ0=sQuery(id+"F0.wireOp",EDGE,"E0.bottom");var subQ1=sQuery(id+"F0.wireOp",EDGE,"E0.right");Q12=makeQuery(id+"F3.boolean.opBoolean","SPLIT",EDGE,{"disambiguationData":[TD([makeQuery(id+"F3.opExtrude","SWEPT_FACE",FACE,{"disambiguationData":[OSD([sQuery(id+"F2.wireOp",EDGE,"E18.MirrorCS")])]})])],"derivedFrom":makeQuery(id+"F1.opExtrude","SWEPT_EDGE",EDGE,{"disambiguationData":[OSD([subQ0,subQ1])]})});}
            var Q13;
            {var subQ0=sQuery(id+"F0.wireOp",EDGE,"E0.right");var subQ1=sQuery(id+"F0.wireOp",EDGE,"E0.top");Q13=makeQuery(id+"F3.boolean.opBoolean","SPLIT",EDGE,{"disambiguationData":[TD([makeQuery(id+"F3.opExtrude","SWEPT_FACE",FACE,{"disambiguationData":[OSD([sQuery(id+"F2.wireOp",EDGE,"E18.MirrorCS")])]})])],"derivedFrom":makeQuery(id+"F1.opExtrude","SWEPT_EDGE",EDGE,{"disambiguationData":[OSD([subQ1,subQ0])]})});}
            var Q14;
            {var subQ0=sQuery(id+"F0.wireOp",EDGE,"E0.left");var subQ1=sQuery(id+"F0.wireOp",EDGE,"E0.top");Q14=makeQuery(id+"F3.boolean.opBoolean","SPLIT",EDGE,{"disambiguationData":[TD([makeQuery(id+"F3.opExtrude","SWEPT_FACE",FACE,{"disambiguationData":[OSD([sQuery(id+"F2.wireOp",EDGE,"E5")])]})])],"derivedFrom":makeQuery(id+"F1.opExtrude","SWEPT_EDGE",EDGE,{"disambiguationData":[OSD([subQ1,subQ0])]})});}
            var Q15;
            {var subQ0=sQuery(id+"F0.wireOp",EDGE,"E0.bottom");var subQ1=sQuery(id+"F0.wireOp",EDGE,"E0.left");Q15=makeQuery(id+"F3.boolean.opBoolean","SPLIT",EDGE,{"disambiguationData":[TD([makeQuery(id+"F3.opExtrude","SWEPT_FACE",FACE,{"disambiguationData":[OSD([sQuery(id+"F2.wireOp",EDGE,"E5")])]})])],"derivedFrom":makeQuery(id+"F1.opExtrude","SWEPT_EDGE",EDGE,{"disambiguationData":[OSD([subQ0,subQ1])]})});}
            fillet(context, id + "F34", {"entities" : qUnion([Q0, Q1, Q2, Q3, Q4, Q5, Q6, Q7, Q8, Q9, Q10, Q11, Q12, Q13, Q14, Q15]), "radius" : 5.08 * mm, "tangentPropagation" : true, "allowEdgeOverflow" : false});
        }
    });
